# Revit family: Drain_Trap_Shallow-Zurn-Z451B
name_source: partatom
category: Plumbing Fixtures
units: mm (PartAtom-declared; Revit-internal decimal feet)

## family parameters
Always vertical = Yes
Cut with Voids When Loaded = No
Maintain Annotation Orientation = No
OmniClass Number = 23.45.55.21
OmniClass Title = Drains (Wastes)
Part Type = Normal
Room Calculation Point = No
Round Connector Dimension = Use Radius
Shared = No
Work Plane-Based = No

## types (14) — shared parameters
Assembly Code = D2030300
CW Connection = No
Default Elevation = 25 "
Description = SHALLOW TRAP DRAIN W/ TYPE B STRAINER
HW Connection = No
Main Material = Iron - Zurn -Cast - Painted - Blue
Manufacturer = Zurn Water, LLC
Manufacurer Brand = Zurn
Modified Date = 11/26/2025
Product Documentation Link = https://files.zurn.com
Product Page URL = https://www.zurn.com
Product data url = https://www.bimobject.com
URL = www.zurn.com
Vent Connection = No
WFU = 1
Waste Connection = Yes
zero-valued in all types: CWFU, HWFU

## per-type parameters (varying)
| type | A_ Pipe Size (Actual-Inner) | A_ Pipe Size (Actual-Outer) | A_ Pipe Size (Nominal) | Approx. Weight (Lbs) | Body Height | Botton Body Radius | Connector radius | Distance from pipe to body | Distance of pipe face | Frame and Grate | Grate Open Area Sq.in | Mid point of pipe | Model | Pipe Body Height | Pipe-2 | Pipe-3 | Strainer Dia_B | Type Comments |
| ZB451B-2IP-5" Strainer | 1.034 " | 1.188 " | 2 " | 15 " | 6.125 " | 1.5 " | 1 " | 4.25 " | 8 " | Bronze - Zurn - Polished | 8 " | 1.438 " | ZB415B | 5.75 " | Yes | No | 5 " | ZB451B-2 Inch Threaded Outlet w/5 inch Strainer |
| ZB451B-2IP-6" Strainer | 1.034 " | 1.188 " | 2 " | 18 " | 6.125 " | 1.5 " | 1 " | 4.25 " | 8 " | Bronze - Zurn - Polished | 9 " | 1.438 " | ZB415B | 5.75 " | Yes | No | 6 " | ZB451B-2 Inch Threaded Outlet w/6 inch Strainer |
| ZB451B-2IP-7" Strainer | 1.034 " | 1.188 " | 2 " | 20 " | 6.125 " | 1.5 " | 1 " | 4.25 " | 8 " | Bronze - Zurn - Polished | 12 " | 1.438 " | ZB415B | 5.75 " | Yes | No | 7 " | ZB451B-2 Inch Threaded Outlet w/7 inch Strainer |
| ZB451B-3IC-5" Strainer | 1.534 " | 1.75 " | 3 " | 15 " | 7.25 " | 1.625 " | 1.5 " | 5.375 " | 8.75 " | Bronze - Zurn - Polished | 8 " | 2 " | ZB415B | 6.75 " | No | Yes | 5 " | ZB451B-3 Inch Threaded Outlet w/5 inch Strainer |
| ZB451B-3IC-6" Strainer | 1.534 " | 1.75 " | 3 " | 18 " | 7.25 " | 1.625 " | 1.5 " | 5.375 " | 8.75 " | Bronze - Zurn - Polished | 9 " | 2 " | ZB415B | 6.75 " | No | Yes | 6 " | ZB451B-3 Inch Threaded Outlet w/6 inch Strainer |
| ZB451B-3IC-7" Strainer | 1.534 " | 1.75 " | 3 " | 20 " | 7.25 " | 1.625 " | 1.5 " | 5.375 " | 8.75 " | Bronze - Zurn - Polished | 12 " | 2 " | ZB415B | 6.75 " | No | Yes | 7 " | ZB451B-3 Inch Threaded Outlet w/7 inch Strainer |
| ZB451B-3IC-8" Strainer | 1.534 " | 1.75 " | 3 " | 21 " | 7.25 " | 1.625 " | 1.5 " | 5.375 " | 8.75 " | Bronze - Zurn - Polished | 18 " | 2 " | ZB415B | 6.75 " | No | Yes | 8 " | ZB451B-3 Inch Threaded Outlet w/8 inch Strainer |
| ZN451B-2IP-5" Strainer | 1.034 " | 1.188 " | 2 " | 15 " | 6.125 " | 1.5 " | 1 " | 4.25 " | 8 " | Bronze - Zurn - Polished Nickel | 8 " | 1.438 " | ZN415B | 5.75 " | Yes | No | 5 " | ZN451B-2 Inch Threaded Outlet w/5 inch Strainer |
| ZN451B-2IP-6" Strainer | 1.034 " | 1.188 " | 2 " | 18 " | 6.125 " | 1.5 " | 1 " | 4.25 " | 8 " | Bronze - Zurn - Polished Nickel | 9 " | 1.438 " | ZN415B | 5.75 " | Yes | No | 6 " | ZN451B-2 Inch Threaded Outlet w/6 inch Strainer |
| ZN451B-2IP-7" Strainer | 1.034 " | 1.188 " | 2 " | 20 " | 6.125 " | 1.5 " | 1 " | 4.25 " | 8 " | Bronze - Zurn - Polished Nickel | 12 " | 1.438 " | ZN415B | 5.75 " | Yes | No | 7 " | ZN451B-2 Inch Threaded Outlet w/7 inch Strainer |
| ZN451B-3IC- 5" Strainer | 1.534 " | 1.75 " | 3 " | 15 " | 7.25 " | 1.625 " | 1.5 " | 5.375 " | 8.75 " | Bronze - Zurn - Polished Nickel | 8 " | 2 " | ZN415B | 6.75 " | No | Yes | 5 " | ZN451B-3 Inch Threaded Outlet w/5 inch Strainer |
| ZN451B-3IC-6" Strainer | 1.534 " | 1.75 " | 3 " | 18 " | 7.25 " | 1.625 " | 1.5 " | 5.375 " | 8.75 " | Bronze - Zurn - Polished Nickel | 9 " | 2 " | ZN415B | 6.75 " | No | Yes | 6 " | ZN451B-3 Inch Threaded Outlet w/6 inch Strainer |
| ZN451B-3IC-7" Strainer | 1.534 " | 1.75 " | 3 " | 20 " | 7.25 " | 1.625 " | 1.5 " | 5.375 " | 8.75 " | Bronze - Zurn - Polished Nickel | 12 " | 2 " | ZN415B | 6.75 " | No | Yes | 7 " | ZN451B-3 Inch Threaded Outlet w/7 inch Strainer |
| ZN451B-3IC-8" Strainer | 1.534 " | 1.75 " | 3 " | 21 " | 7.25 " | 1.625 " | 1.5 " | 5.375 " | 8.75 " | Bronze - Zurn - Polished Nickel | 18 " | 2 " | ZN415B | 6.75 " | No | Yes | 8 " | ZN451B-3 Inch Threaded Outlet w/8 inch Strainer |

## geometry (parser evidence)
native form markers: Sweep x10
no freeform markers — native parametric forms only
